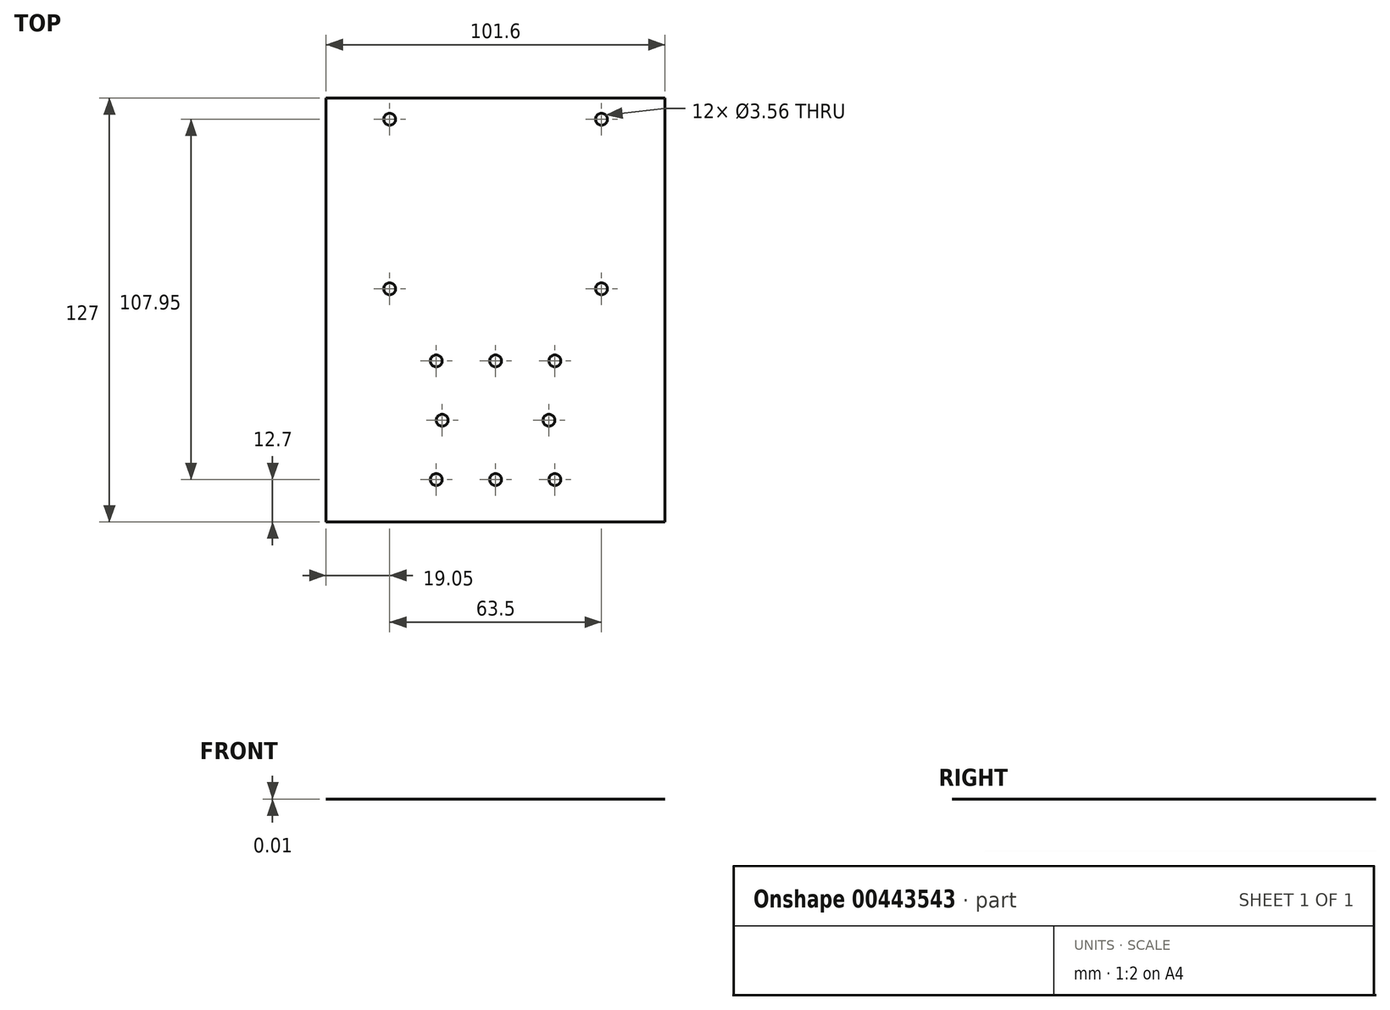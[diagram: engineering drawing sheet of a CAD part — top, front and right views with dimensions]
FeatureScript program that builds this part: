
annotation { "Feature Type Name" : "Feature", "Feature Type Description" : "" }
export const myFeature = defineFeature(function(context is Context, id is Id, definition is map)
    precondition{}
    {
        {
            var Q0;
            Q0=qCreatedBy(makeId("Top.planeOp"),FACE);
            var sketch = newSketch(context, id + "F0", { "sketchPlane" : qUnion([Q0])});
            skLineSegment(sketch, "E0.bottom", {"start": v(0, 0) * mm, "end": v(101.6, 0) * mm});
            skLineSegment(sketch, "E0.top", {"start": v(0, 127) * mm, "end": v(101.6, 127) * mm});
            skLineSegment(sketch, "E0.left", {"start": v(0, 0) * mm, "end": v(0, 127) * mm});
            skLineSegment(sketch, "E0.right", {"start": v(101.6, 0) * mm, "end": v(101.6, 127) * mm});
            skCircle(sketch, "E1", {"center": v(33.02, 12.7) * mm, "radius": 1.78 * mm});
            skCircle(sketch, "E2.0.1.0", {"center": v(33.02, 48.26) * mm, "radius": 1.78 * mm});
            skCircle(sketch, "E2.1.0.0", {"center": v(50.8, 12.7) * mm, "radius": 1.78 * mm});
            skCircle(sketch, "E2.1.1.0", {"center": v(50.8, 48.26) * mm, "radius": 1.78 * mm});
            skCircle(sketch, "E2.2.0.0", {"center": v(68.58, 12.7) * mm, "radius": 1.78 * mm});
            skCircle(sketch, "E2.2.1.0", {"center": v(68.58, 48.26) * mm, "radius": 1.78 * mm});
            skLineSegment(sketch, "E2.direction1", {"start": v(33.02, 12.7) * mm, "end": v(50.8, 12.7) * mm, "construction": true});
            skLineSegment(sketch, "E2.direction2", {"start": v(33.02, 12.7) * mm, "end": v(33.02, 48.26) * mm, "construction": true});
            skCircle(sketch, "E3", {"center": v(34.8, 30.48) * mm, "radius": 1.78 * mm});
            skCircle(sketch, "E4", {"center": v(66.8, 30.48) * mm, "radius": 1.78 * mm});
            skPoint(sketch, "E5", {"position": v(50.8, 0) * mm});
            skCircle(sketch, "E6", {"center": v(19.05, 69.85) * mm, "radius": 1.78 * mm});
            skLineSegment(sketch, "E7", {"start": v(19.05, 69.85) * mm, "end": v(82.55, 69.85) * mm, "construction": true});
            skCircle(sketch, "E8", {"center": v(82.55, 69.85) * mm, "radius": 1.78 * mm});
            skPoint(sketch, "E9", {"position": v(50.8, 69.85) * mm});
            skLineSegment(sketch, "E10", {"start": v(101.6, 95.25) * mm, "end": v(0, 95.25) * mm, "construction": true});
            skCircle(sketch, "E11.MirrorC", {"center": v(19.05, 120.65) * mm, "radius": 1.78 * mm});
            skCircle(sketch, "E12.MirrorC", {"center": v(82.55, 120.65) * mm, "radius": 1.78 * mm});
            skSolve(sketch);
        }
        {
            var Q0;
            Q0=makeQuery(id+"F0.imprint","IMPRINT",FACE,{"disambiguationData":[TD([[makeQuery(id+"F0.imprint","IMPRINT",EDGE,{"derivedFrom":sQuery(id+"F0.wireOp",EDGE,"E0.bottom")}),1.0]])]});
            extrude(context, id + "F1", {"entities" : qUnion([Q0]), "depth" : 1 / 101.6 * mm});
        }
    });
